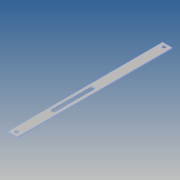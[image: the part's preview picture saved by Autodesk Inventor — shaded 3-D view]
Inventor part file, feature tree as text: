
AUTODESK INVENTOR PART (.ipt)
format: ipt  version: 2019 (Build 230136000, 136)  size: 99,840 bytes
history: native  units: mm
features: sketch x3, extrude x2, hole x1
ambient origin geometry x8: Origin, YZ Plane, XZ Plane, XY Plane, X Axis, Y Axis, Z Axis, Center Point
bodies: Solide1 (feature_tree)
feature tree (6):
  extrude  "Extrusion1"  Depth=226.0mm
  hole  "Perçage1"  [1 undecoded]
  extrude  "Extrusion2"  Depth=1.0mm TaperAngle=0.0deg
  sketch  "Esquisse2"
  sketch  "Esquisse3"
  sketch  "Esquisse4"
note: 1 required parameter value undecoded (feature->parameter linkage not recoverable at this tier; creation-order binding heuristic only, values carry confidence <= 0.55)
